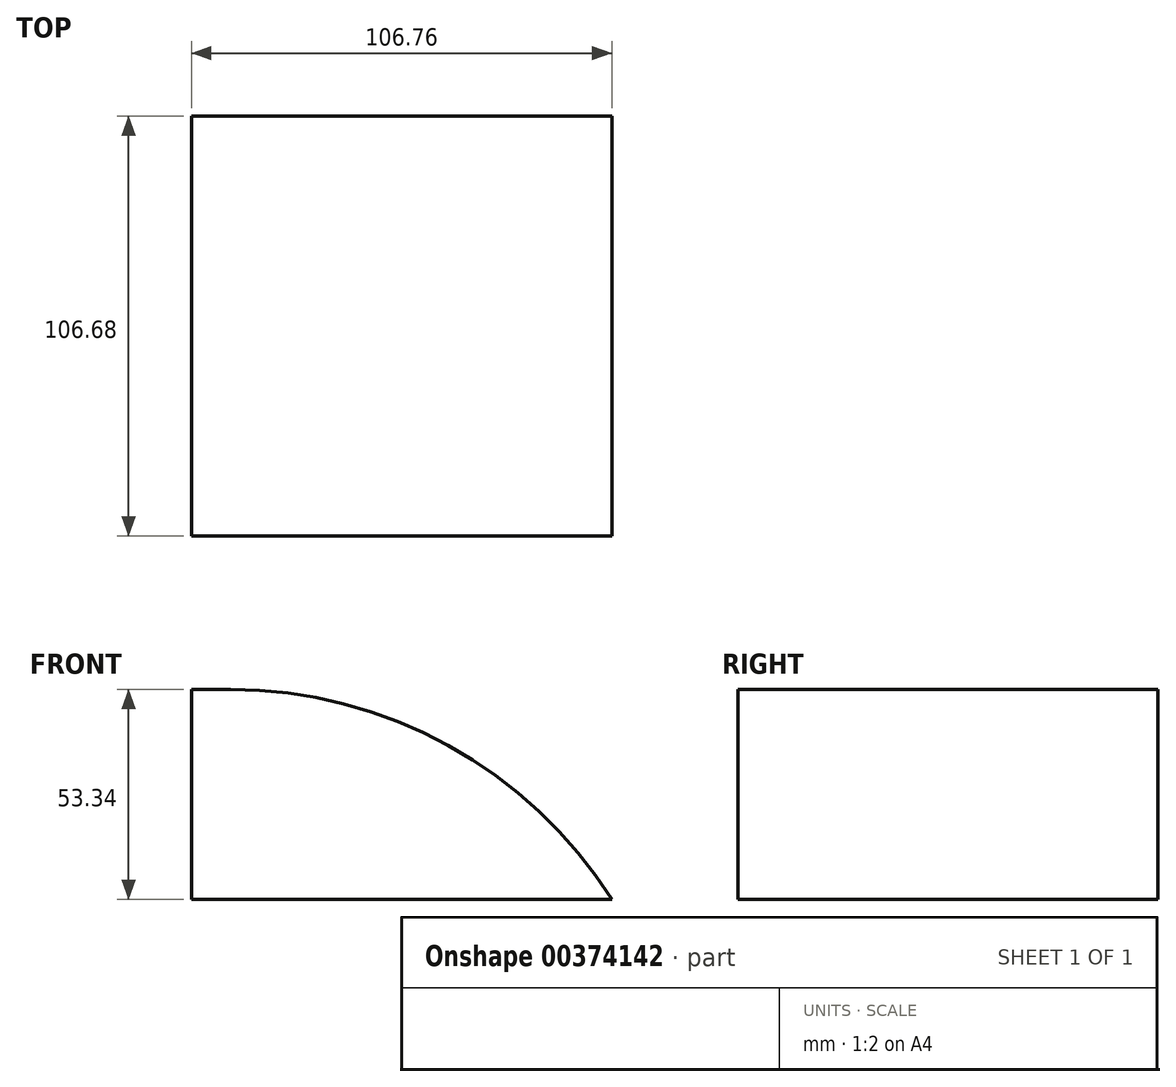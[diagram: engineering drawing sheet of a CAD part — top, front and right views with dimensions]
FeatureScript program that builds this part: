
annotation { "Feature Type Name" : "Feature", "Feature Type Description" : "" }
export const myFeature = defineFeature(function(context is Context, id is Id, definition is map)
    precondition{}
    {
        {
            var Q0;
            Q0=qCreatedBy(makeId("Front.planeOp"),FACE);
            var sketch = newSketch(context, id + "F0", { "sketchPlane" : qUnion([Q0])});
            skLineSegment(sketch, "E0", {"start": v(0, 0) * mm, "end": v(0, 53.34) * mm});
            skLineSegment(sketch, "E1", {"start": v(0, 53.34) * mm, "end": v(-53.38, 53.34) * mm});
            skLineSegment(sketch, "E2", {"start": v(-53.38, 53.34) * mm, "end": v(-53.38, 0) * mm});
            skLineSegment(sketch, "E3", {"start": v(-53.38, 0) * mm, "end": v(0, 0) * mm});
            skSolve(sketch);
        }
        {
            var Q0;
            Q0=makeQuery(id+"F0.imprint","IMPRINT",FACE,{"disambiguationData":[TD([[makeQuery(id+"F0.imprint","IMPRINT",EDGE,{"derivedFrom":sQuery(id+"F0.wireOp",EDGE,"E0")}),1.0]])]});
            extrude(context, id + "F1", {"entities" : qUnion([Q0]), "depth" : 53.34 * mm});
        }
        {
            var Q0;
            Q0=makeQuery(id+"F1.opExtrude","SWEPT_BODY",BODY,{"disambiguationData":[OSD([sQuery(id+"F0.wireOp",EDGE,"E0"),sQuery(id+"F0.wireOp",EDGE,"E1"),sQuery(id+"F0.wireOp",EDGE,"E2"),sQuery(id+"F0.wireOp",EDGE,"E3")])]});
            var Q1;
            Q1=qCreatedBy(makeId("Right.planeOp"),FACE);
            mirror(context, id + "F2", {"operationType" : NewBodyOperationType.ADD, "entities" : qUnion([Q0]), "mirrorPlane" : qUnion([Q1])});
        }
        {
            var Q0;
            Q0=makeQuery(id+"F1.opExtrude","SWEPT_BODY",BODY,{"disambiguationData":[OSD([sQuery(id+"F0.wireOp",EDGE,"E0"),sQuery(id+"F0.wireOp",EDGE,"E1"),sQuery(id+"F0.wireOp",EDGE,"E2"),sQuery(id+"F0.wireOp",EDGE,"E3")])]});
            var Q1;
            {var subQ0=makeQuery(id+"F1.opExtrude","CAP_FACE",FACE,{"disambiguationData":[OSD([sQuery(id+"F0.wireOp",EDGE,"E0"),sQuery(id+"F0.wireOp",EDGE,"E1"),sQuery(id+"F0.wireOp",EDGE,"E2"),sQuery(id+"F0.wireOp",EDGE,"E3")])],"isStart":false});Q1=makeQuery(id+"F2.boolean.opBoolean","MERGE",FACE,{"derivedFrom":[subQ0,makeQuery(id+"F2.opPattern","COPY",FACE,{"derivedFrom":subQ0,"instanceName":"1"})]});}
            mirror(context, id + "F3", {"operationType" : NewBodyOperationType.ADD, "entities" : qUnion([Q0]), "mirrorPlane" : qUnion([Q1])});
        }
        {
            var Q0;
            {var subQ0=makeQuery(id+"F2.opPattern","COPY",EDGE,{"derivedFrom":makeQuery(id+"F1.opExtrude","SWEPT_EDGE",EDGE,{"disambiguationData":[OSD([sQuery(id+"F0.wireOp",EDGE,"E1"),sQuery(id+"F0.wireOp",EDGE,"E2")])]}),"instanceName":"1"});Q0=makeQuery(id+"F3.boolean.opBoolean","MERGE",EDGE,{"derivedFrom":[subQ0,makeQuery(id+"F3.opPattern","COPY",EDGE,{"derivedFrom":subQ0,"instanceName":"1"})]});}
            fillet(context, id + "F4", {"entities" : qUnion([Q0]), "radius" : 114.67 * mm, "tangentPropagation" : true, "allowEdgeOverflow" : false});
        }
    });
